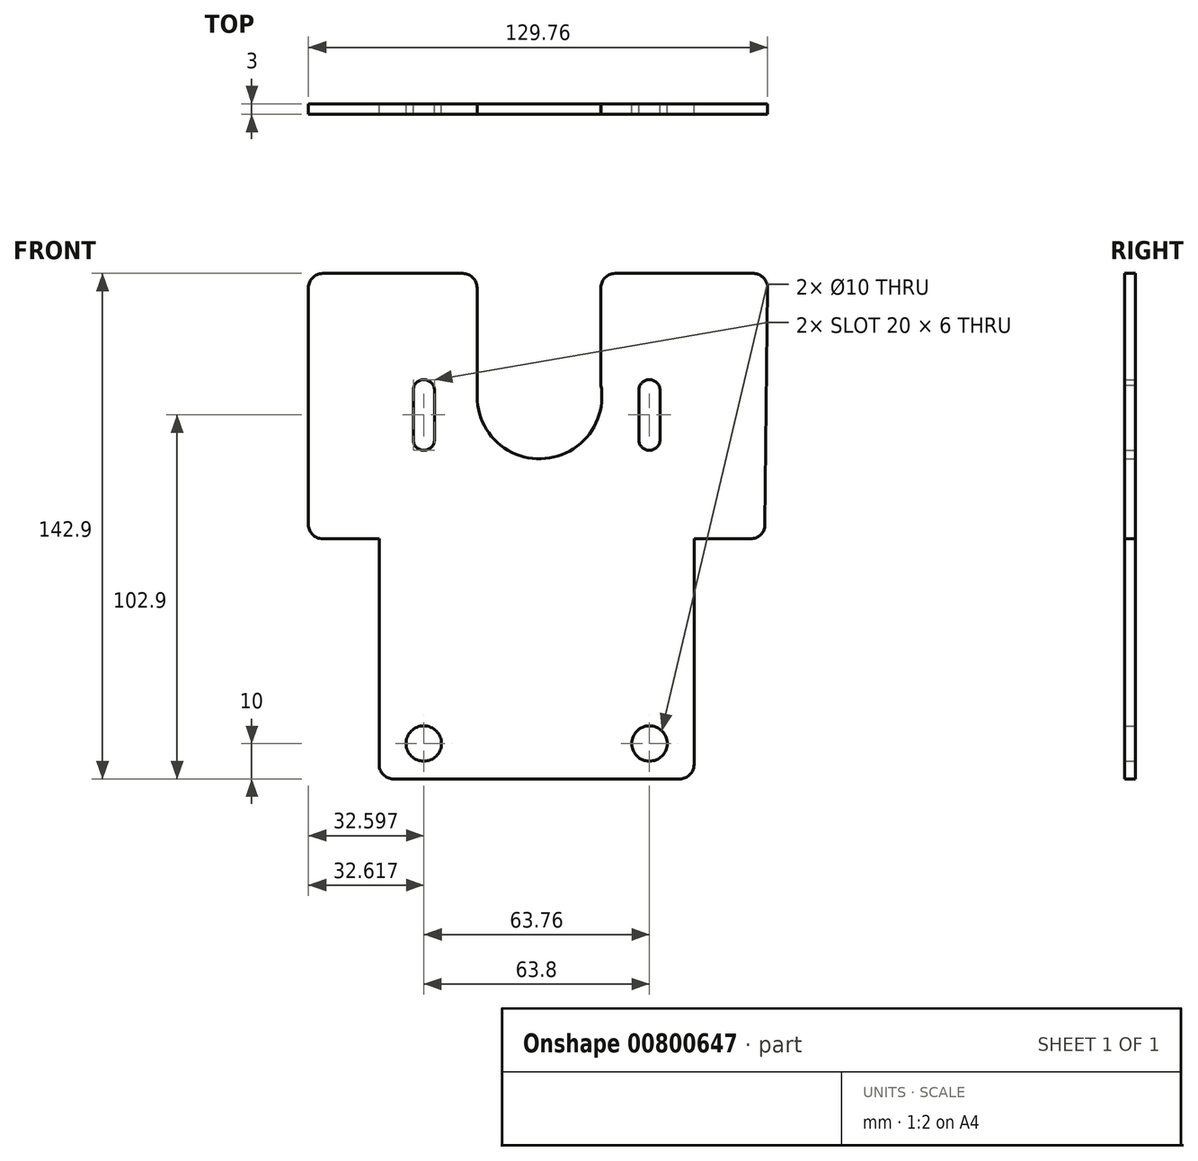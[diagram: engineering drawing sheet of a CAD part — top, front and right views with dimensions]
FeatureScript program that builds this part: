
annotation { "Feature Type Name" : "Feature", "Feature Type Description" : "" }
export const myFeature = defineFeature(function(context is Context, id is Id, definition is map)
    precondition{}
    {
        {
            var Q0;
            Q0=qCreatedBy(makeId("Front.planeOp"),FACE);
            var sketch = newSketch(context, id + "F0", { "sketchPlane" : qUnion([Q0])});
            skLineSegment(sketch, "E0", {"start": v(-4.04, 0) * mm, "end": v(-43.15, 0) * mm});
            skLineSegment(sketch, "E1", {"start": v(-129.8, -4) * mm, "end": v(-129.8, -71) * mm});
            skLineSegment(sketch, "E2", {"start": v(-125.8, -75) * mm, "end": v(-109.8, -75) * mm});
            skLineSegment(sketch, "E3", {"start": v(-109.8, -75) * mm, "end": v(-109.8, -138.9) * mm});
            skLineSegment(sketch, "E4", {"start": v(-105.8, -142.9) * mm, "end": v(-24.8, -142.9) * mm});
            skLineSegment(sketch, "E5", {"start": v(-20.8, -138.9) * mm, "end": v(-20.8, -75) * mm});
            skLineSegment(sketch, "E6", {"start": v(-20.8, -75) * mm, "end": v(-4.76, -75) * mm});
            skLineSegment(sketch, "E7", {"start": v(-0.76, -71.04) * mm, "end": v(-0.04, -4.04) * mm});
            skLineSegment(sketch, "E8", {"start": v(-125.8, 0) * mm, "end": v(-86.15, 0) * mm, "construction": true});
            skArc(sketch, "E9", {"start": v(-82.15, -34.75) * mm, "mid": v(-62.87, -52.32) * mm, "end": v(-47.15, -31.5) * mm});
            skLineSegment(sketch, "E10", {"start": v(-109.8, -75) * mm, "end": v(-65.3, -75) * mm, "construction": true});
            skLineSegment(sketch, "E11", {"start": v(-65.3, -75) * mm, "end": v(-65.3, -52.4) * mm, "construction": true});
            skLineSegment(sketch, "E12", {"start": v(-82.15, -34.75) * mm, "end": v(-82.15, -4) * mm});
            skLineSegment(sketch, "E13", {"start": v(-47.15, -4) * mm, "end": v(-47.15, -34.75) * mm});
            skPoint(sketch, "E14.orphan", {"position": v(-64.9, 0) * mm});
            skLineSegment(sketch, "E15.trimOffspring", {"start": v(-82.15, 0) * mm, "end": v(-129.8, 0) * mm});
            skLineSegment(sketch, "E16", {"start": v(-129.8, 0) * mm, "end": v(-97.18, 0) * mm, "construction": true});
            skLineSegment(sketch, "E17", {"start": v(-97.18, 0) * mm, "end": v(-97.18, -30) * mm, "construction": true});
            skPoint(sketch, "E18.visualSharp", {"position": v(-129.8, 0) * mm});
            skArc(sketch, "E18.filletArc", {"start": v(-125.8, 0) * mm, "mid": v(-128.63, -1.17) * mm, "end": v(-129.8, -4) * mm});
            skPoint(sketch, "E19.visualSharp", {"position": v(-129.8, -75) * mm});
            skArc(sketch, "E19.filletArc", {"start": v(-129.8, -71) * mm, "mid": v(-128.63, -73.83) * mm, "end": v(-125.8, -75) * mm});
            skPoint(sketch, "E20.visualSharp", {"position": v(-82.15, 0) * mm});
            skArc(sketch, "E20.filletArc", {"start": v(-82.15, -4) * mm, "mid": v(-83.32, -1.17) * mm, "end": v(-86.15, 0) * mm});
            skPoint(sketch, "E21.visualSharp", {"position": v(-47.15, 0) * mm});
            skArc(sketch, "E21.filletArc", {"start": v(-43.15, 0) * mm, "mid": v(-45.98, -1.17) * mm, "end": v(-47.15, -4) * mm});
            skPoint(sketch, "E22.visualSharp", {"position": v(0, 0) * mm});
            skArc(sketch, "E22.filletArc", {"start": v(-0.04, -4.04) * mm, "mid": v(-1.2, -1.19) * mm, "end": v(-4.04, 0) * mm});
            skPoint(sketch, "E23.visualSharp", {"position": v(-0.8, -75) * mm});
            skArc(sketch, "E23.filletArc", {"start": v(-4.76, -75) * mm, "mid": v(-1.95, -73.84) * mm, "end": v(-0.76, -71.04) * mm});
            skPoint(sketch, "E24.visualSharp", {"position": v(-20.8, -142.9) * mm});
            skArc(sketch, "E24.filletArc", {"start": v(-24.8, -142.9) * mm, "mid": v(-21.97, -141.73) * mm, "end": v(-20.8, -138.9) * mm});
            skPoint(sketch, "E25.visualSharp", {"position": v(-109.8, -142.9) * mm});
            skArc(sketch, "E25.filletArc", {"start": v(-109.8, -138.9) * mm, "mid": v(-108.63, -141.73) * mm, "end": v(-105.8, -142.9) * mm});
            skArc(sketch, "E26", {"start": v(-94.18, -33) * mm, "mid": v(-97.18, -30) * mm, "end": v(-100.18, -33) * mm});
            skArc(sketch, "E27", {"start": v(-100.18, -47) * mm, "mid": v(-97.18, -50) * mm, "end": v(-94.18, -47) * mm});
            skLineSegment(sketch, "E28", {"start": v(-94.18, -33) * mm, "end": v(-94.18, -47) * mm});
            skLineSegment(sketch, "E29", {"start": v(-100.18, -47) * mm, "end": v(-100.18, -33) * mm});
            skLineSegment(sketch, "E30", {"start": v(-109.8, -142.9) * mm, "end": v(-97.2, -142.9) * mm, "construction": true});
            skLineSegment(sketch, "E31", {"start": v(-97.2, -142.9) * mm, "end": v(-97.2, -132.9) * mm, "construction": true});
            skCircle(sketch, "E32", {"center": v(-97.2, -132.9) * mm, "radius": 5 * mm});
            skArc(sketch, "E33.MirrorCS", {"start": v(-20.8, -138.9) * mm, "mid": v(-21.97, -141.73) * mm, "end": v(-24.8, -142.9) * mm});
            skLineSegment(sketch, "E34.MirrorCS", {"start": v(-33.4, -142.9) * mm, "end": v(-33.4, -132.9) * mm, "construction": true});
            skLineSegment(sketch, "E35.MirrorCS", {"start": v(-20.8, -142.9) * mm, "end": v(-33.4, -142.9) * mm, "construction": true});
            skArc(sketch, "E36.MirrorCS", {"start": v(-36.42, -33) * mm, "mid": v(-33.42, -30) * mm, "end": v(-30.42, -33) * mm});
            skLineSegment(sketch, "E37.MirrorCS", {"start": v(-24.8, -142.9) * mm, "end": v(-105.8, -142.9) * mm});
            skLineSegment(sketch, "E38.MirrorCS", {"start": v(-30.42, -47) * mm, "end": v(-30.42, -33) * mm});
            skLineSegment(sketch, "E39.MirrorCS", {"start": v(-20.8, -75) * mm, "end": v(-20.8, -138.9) * mm});
            skLineSegment(sketch, "E40.MirrorCS", {"start": v(-33.42, 0) * mm, "end": v(-33.42, -30) * mm, "construction": true});
            skCircle(sketch, "E41.MirrorC", {"center": v(-33.4, -132.9) * mm, "radius": 5 * mm});
            skLineSegment(sketch, "E42.MirrorCS", {"start": v(-36.42, -33) * mm, "end": v(-36.42, -47) * mm});
            skArc(sketch, "E43.MirrorCS", {"start": v(-30.42, -47) * mm, "mid": v(-33.42, -50) * mm, "end": v(-36.42, -47) * mm});
            skLineSegment(sketch, "E44.MirrorCS", {"start": v(-20.8, -75) * mm, "end": v(-65.3, -75) * mm, "construction": true});
            skLineSegment(sketch, "E45.MirrorCS", {"start": v(-4.8, -75) * mm, "end": v(-20.8, -75) * mm});
            skSolve(sketch);
        }
        {
            var Q0;
            Q0=makeQuery(id+"F0.imprint","IMPRINT",FACE,{"disambiguationData":[TD([[makeQuery(id+"F0.imprint","IMPRINT",EDGE,{"derivedFrom":sQuery(id+"F0.wireOp",EDGE,"E0")}),1.0]])]});
            extrude(context, id + "F1", {"entities" : qUnion([Q0]), "depth" : 3 * mm, "offsetDistance" : 25 * mm});
        }
    });
